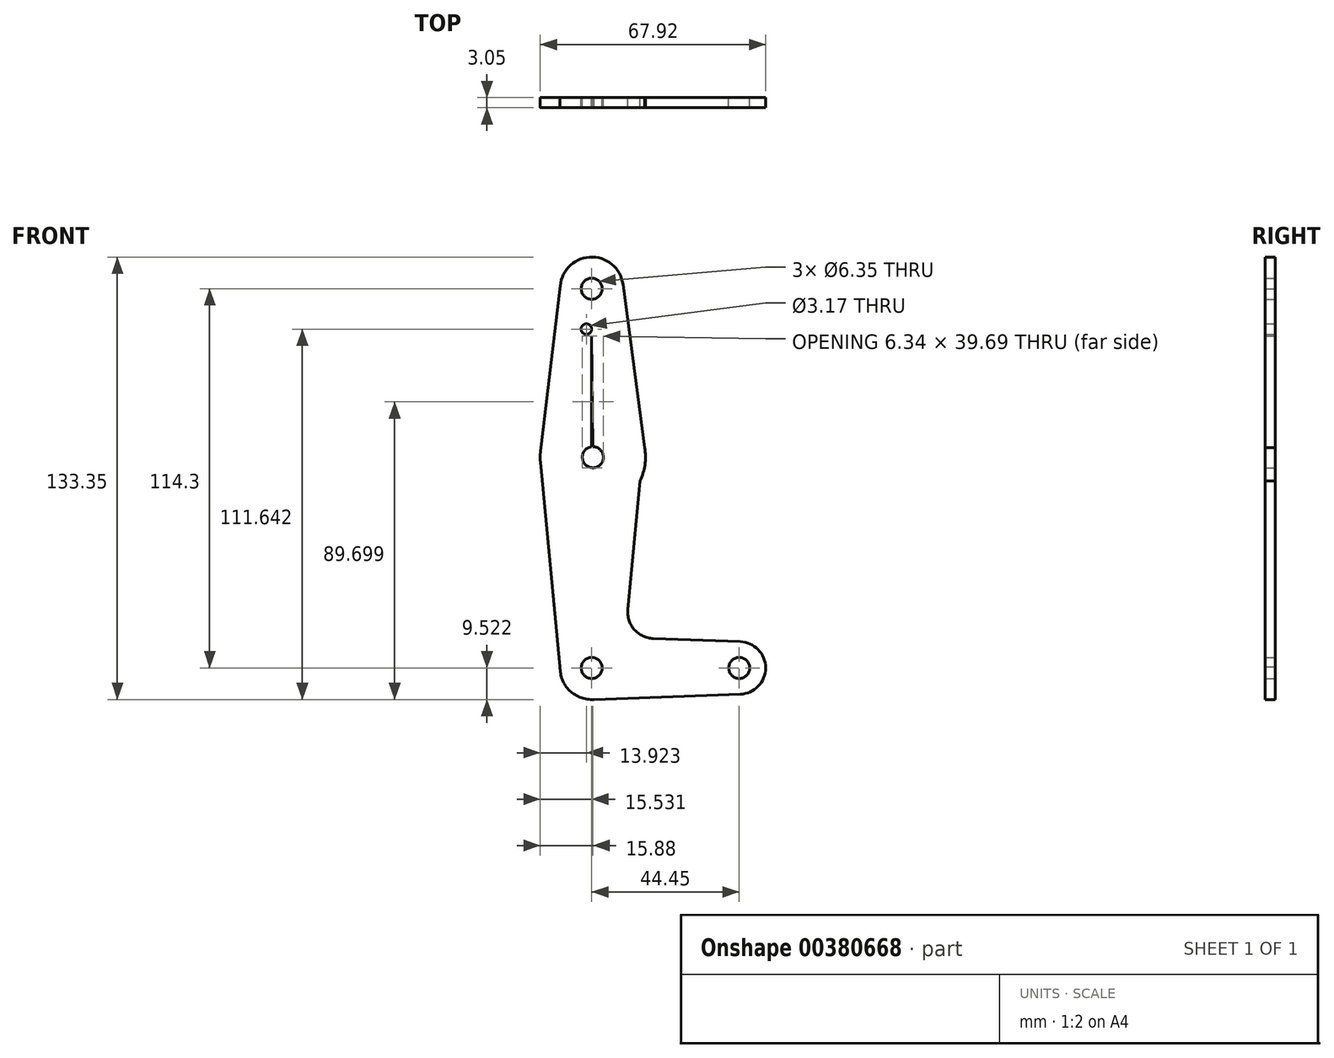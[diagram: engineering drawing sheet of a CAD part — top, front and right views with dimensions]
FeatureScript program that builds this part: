
annotation { "Feature Type Name" : "Feature", "Feature Type Description" : "" }
export const myFeature = defineFeature(function(context is Context, id is Id, definition is map)
    precondition{}
    {
        {
            var Q0;
            Q0=qCreatedBy(makeId("Front.planeOp"),FACE);
            var sketch = newSketch(context, id + "F0", { "sketchPlane" : qUnion([Q0])});
            skLineSegment(sketch, "E0", {"start": v(0, 52.32) * mm, "end": v(0, -61.98) * mm});
            skLineSegment(sketch, "E1", {"start": v(0, -61.98) * mm, "end": v(44.44, -61.98) * mm});
            skCircle(sketch, "E2", {"center": v(0, 52.32) * mm, "radius": 9.53 * mm});
            skCircle(sketch, "E3", {"center": v(0, -61.98) * mm, "radius": 9.53 * mm});
            skCircle(sketch, "E4", {"center": v(0.34, 1.52) * mm, "radius": 15.88 * mm});
            skCircle(sketch, "E5", {"center": v(44.44, -61.98) * mm, "radius": 7.94 * mm});
            skLineSegment(sketch, "E6", {"start": v(0, -61.98) * mm, "end": v(0, 1.52) * mm});
            skLineSegment(sketch, "E7", {"start": v(0, -71.5) * mm, "end": v(44.72, -69.91) * mm});
            skLineSegment(sketch, "E8", {"start": v(44.72, -54.05) * mm, "end": v(18.5, -53.1) * mm});
            skLineSegment(sketch, "E9", {"start": v(15.95, 4.38) * mm, "end": v(9.43, 53.57) * mm});
            skLineSegment(sketch, "E10", {"start": v(15.02, 0) * mm, "end": v(10.88, -44.42) * mm});
            skLineSegment(sketch, "E11", {"start": v(-9.53, -61.64) * mm, "end": v(-15.47, 0) * mm});
            skLineSegment(sketch, "E12", {"start": v(-9.24, 54.66) * mm, "end": v(-15.43, 3.42) * mm});
            skCircle(sketch, "E13", {"center": v(0, 52.32) * mm, "radius": 3.18 * mm});
            skCircle(sketch, "E14", {"center": v(0.34, 1.52) * mm, "radius": 3.18 * mm});
            skCircle(sketch, "E15", {"center": v(0, -61.98) * mm, "radius": 0.32 * mm});
            skCircle(sketch, "E16", {"center": v(44.44, -61.98) * mm, "radius": 0.32 * mm});
            skPoint(sketch, "E17.newPointA", {"position": v(9.43, -59.88) * mm});
            skPoint(sketch, "E17.newPointB", {"position": v(0, -52.45) * mm});
            skArc(sketch, "E17.filletArc", {"start": v(10.88, -44.42) * mm, "mid": v(12.82, -50.41) * mm, "end": v(18.5, -53.1) * mm});
            skLineSegment(sketch, "E18", {"start": v(0.34, 1.52) * mm, "end": v(0, 38.05) * mm});
            skCircle(sketch, "E19", {"center": v(-1.62, 40.14) * mm, "radius": 1.59 * mm});
            skCircle(sketch, "E20", {"center": v(0, -61.98) * mm, "radius": 3.18 * mm});
            skCircle(sketch, "E21", {"center": v(44.44, -61.98) * mm, "radius": 3.18 * mm});
            skSolve(sketch);
        }
        {
            var Q0;
            Q0 = qSketchRegion(id + "F0", true);
            var Q1;
            {var subQ0=sQuery(id+"F0.wireOp",EDGE,"E20");var subQ1=sQuery(id+"F0.wireOp",EDGE,"E1");var subQ2=makeQuery(id+"F0.imprint","INTERSECT",VERTEX,{"derivedFrom":[subQ1,subQ0]});Q1=makeQuery(id+"F0.imprint","IMPRINT",FACE,{"disambiguationData":[TD([[makeQuery(id+"F0.imprint","IMPRINT",EDGE,{"disambiguationData":[TD([[subQ2,-1.0]])],"derivedFrom":subQ1}),1.0]])]});}
            extrude(context, id + "F1", {"entities" : qUnion([Q0, Q1]), "depth" : 3.05 * mm});
        }
    });
